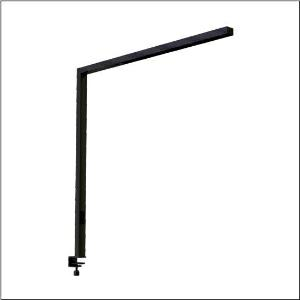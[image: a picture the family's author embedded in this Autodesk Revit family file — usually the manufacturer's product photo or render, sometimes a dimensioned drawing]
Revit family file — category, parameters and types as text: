
# Revit family: silica_31_desk_51my52gatcb
name_source: partatom
category: Lighting Fixtures
units: mm (PartAtom-declared; Revit-internal decimal feet)

## family parameters
Cut with Voids When Loaded = No
Host = Face
Light Source = No
Part Type = Normal
Room Calculation Point = No
Round Connector Dimension = Use Diameter
Shared = No

## types (1)
- --- (1 x LED, 8520 lm, 71 W, 4000K)
    Apparent Load = 71 VA
    CIE Flux Codes = 86 100 100 24 100
    Color Rendering = 80
    Color Temperature = 4000K
    Default Elevation = 1800 mm
    Description = Silica® 31 Desk, desktop luminaire, secondary optical cover: cover panel, of PMMA, light emission: direct/indirect distribution, primary light characteristic: symmetric, installation type: as desk luminaire, LED, rated luminous flux: 8.520lm, luminous efficacy: 120lm/W, light colour: 8tw, colour temperature: 2700..6500K, control gear: Touchdim, daylight-dependent control, with cable with plug, mains connection: 230V, AC, 50Hz, connection cable included, cable length: 2,5m, rated input power: 71W, luminaire head, of aluminium, jet black (RAL 9005), length: 1.203mm, width: 52mm, supporting column, angular, of aluminium, jet black (RAL 9005), baseplate, of steel, jet black (RAL 9005), local control - self-sufficient standalone sensors, direct and indirect component separately switchable, protection rating (complete): IP20, insulation class (complete): insulation class I (protective earthing), certification: CE, ENEC, permissible operating ambient temperature: -20..+40°C, standard: EN 50419, packaging unit: 1 piece
    Height = 36 mm
    Lamp = 1 x LED
    Lamp Light Flux = 8520 lm
    Lamp Power = 71 W
    Lamp count = 1
    Length = 1203 mm
    Luminous efficacy = 120 lm/W
    Manufacturer = Siteco
    ModVariant = No
    Model = 51MY52GATCB
    Mounting Place = Floor
    Mounting Type = Freestanding
    Number of Poles = 1
    OnlyDefault = Yes
    Power Factor = 1
    Product Name = Silica 31 Desk
    Product group = desktop luminaire
    ProductGroupID = 1303
    Protection Class = Protection class I
    Protection Degree = IP 20
    RLX_Detail_Level = 1
    RLX_Emergency_Light_Flux = 0 lm
    RLX_Emergency_Type = 0
    RLX_Emergency_Type_DB = No
    RlxData = <blob elided: 19301 chars, md5=5b810c34>
    Socket = socket
    Standby Power = 0 W
    System Light Flux = 8520 lm
    System Power = 71 W
    Type Comments = factory setting
    Type Image = l_1275329.jpg
    URL = http://relux.com
    VarID = @adj_088669
    Voltage = 0 V
    Weight = 0.00 kg
    Width = 52 mm  [stored 0.170604 ft]

note: [stored X ft] marks values corroborated as IEEE doubles in the binary element streams (Revit-internal decimal feet)

## geometry (parser evidence)
native form markers: Blend x4, Sweep x15
no freeform markers — native parametric forms only
